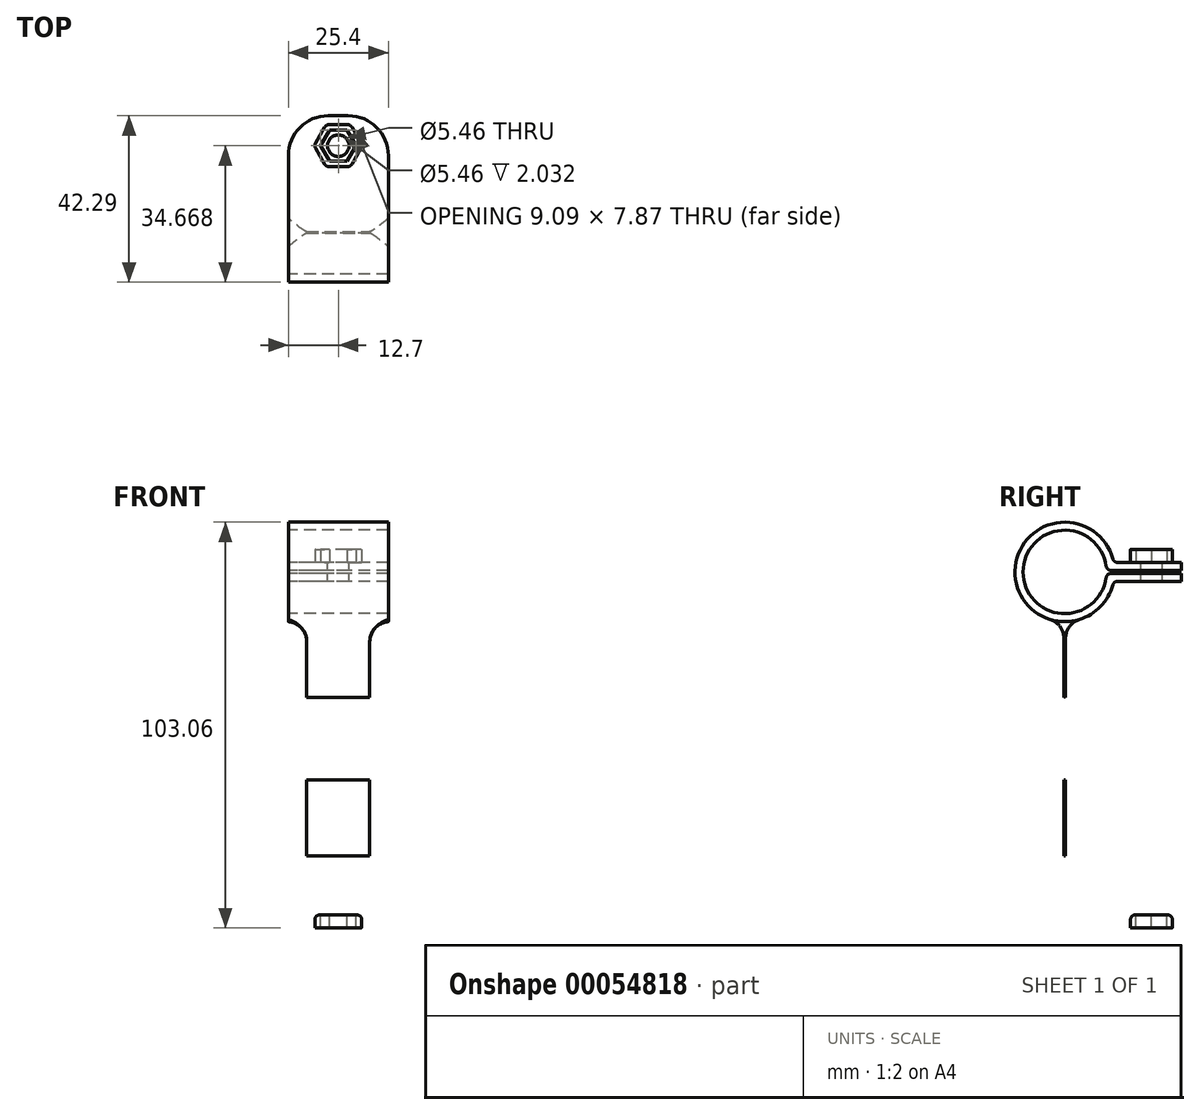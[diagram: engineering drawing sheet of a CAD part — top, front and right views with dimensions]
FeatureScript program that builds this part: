
annotation { "Feature Type Name" : "Feature", "Feature Type Description" : "" }
export const myFeature = defineFeature(function(context is Context, id is Id, definition is map)
    precondition{}
    {
        {
            var Q0;
            Q0=qCreatedBy(makeId("Front.planeOp"),FACE);
            var sketch = newSketch(context, id + "F0", { "sketchPlane" : qUnion([Q0])});
            skLineSegment(sketch, "E0", {"start": v(-8, -29.85) * mm, "end": v(-8, 29.84) * mm});
            skLineSegment(sketch, "E1", {"start": v(-8, 29.85) * mm, "end": v(8, 29.85) * mm});
            skLineSegment(sketch, "E2", {"start": v(8, 29.84) * mm, "end": v(8, -29.85) * mm});
            skCircle(sketch, "E3", {"center": v(0, 0) * mm, "radius": 2.54 * mm});
            skLineSegment(sketch, "E4", {"start": v(-8, -29.85) * mm, "end": v(8, -29.85) * mm});
            skLineSegment(sketch, "E5", {"start": v(-8, 0) * mm, "end": v(8, 0) * mm, "construction": true});
            skSolve(sketch);
        }
        {
            var Q0;
            Q0=qSketchRegion(id+"F0",true);
            extrude(context, id + "F1", {"entities" : qUnion([Q0]), "depth" : ((.116 * 2 + .13) / 2) * mm, "hasSecondDirection" : true, "secondDirectionOppositeDirection" : true, "secondDirectionDepth" : ((.116 * 2 + .13) / 2) * mm});
        }
        {
            var Q0;
            Q0=qCreatedBy(makeId("Right.planeOp"),FACE);
            var sketch = newSketch(context, id + "F2", { "sketchPlane" : qUnion([Q0])});
            skArc(sketch, "E6", {"start": v(10.5, 43.83) * mm, "mid": v(-10.6, 42.35) * mm, "end": v(10.5, 40.88) * mm});
            skArc(sketch, "E7", {"start": v(12.19, 45.7) * mm, "mid": v(-12.64, 42.35) * mm, "end": v(12.19, 39) * mm});
            skLineSegment(sketch, "E8.bottom", {"start": v(13.4, 44.77) * mm, "end": v(29.65, 44.77) * mm});
            skLineSegment(sketch, "E8.top", {"start": v(13.4, 39.94) * mm, "end": v(29.65, 39.94) * mm});
            skLineSegment(sketch, "E8.right", {"start": v(29.65, 44.77) * mm, "end": v(29.65, 42.74) * mm});
            skLineSegment(sketch, "E9.bottom", {"start": v(11.76, 42.74) * mm, "end": v(29.65, 42.74) * mm});
            skLineSegment(sketch, "E9.top", {"start": v(11.76, 41.97) * mm, "end": v(29.65, 41.97) * mm});
            skLineSegment(sketch, "E10.trimOffspring", {"start": v(29.65, 41.97) * mm, "end": v(29.65, 39.94) * mm});
            skLineSegment(sketch, "E11", {"start": v(0, 42.35) * mm, "end": v(10.6, 42.35) * mm, "construction": true});
            skLineSegment(sketch, "E12", {"start": v(10.6, 42.74) * mm, "end": v(10.6, 41.97) * mm, "construction": true});
            skPoint(sketch, "E13.visualSharp", {"position": v(10.6, 42.74) * mm});
            skArc(sketch, "E13.filletArc", {"start": v(10.5, 43.83) * mm, "mid": v(10.93, 43.05) * mm, "end": v(11.76, 42.74) * mm});
            skPoint(sketch, "E14.visualSharp", {"position": v(10.6, 41.97) * mm});
            skArc(sketch, "E14.filletArc", {"start": v(11.76, 41.97) * mm, "mid": v(10.93, 41.66) * mm, "end": v(10.5, 40.88) * mm});
            skPoint(sketch, "E15.visualSharp", {"position": v(12.4, 44.77) * mm});
            skArc(sketch, "E15.filletArc", {"start": v(12.19, 45.7) * mm, "mid": v(12.64, 45.03) * mm, "end": v(13.4, 44.77) * mm});
            skPoint(sketch, "E16.visualSharp", {"position": v(12.4, 39.94) * mm});
            skArc(sketch, "E16.filletArc", {"start": v(13.4, 39.94) * mm, "mid": v(12.64, 39.68) * mm, "end": v(12.19, 39) * mm});
            skLineSegment(sketch, "E17", {"start": v(0, 0) * mm, "end": v(-15.6, 0) * mm, "construction": true});
            skArc(sketch, "E18.MirrorCS", {"start": v(13.4, -39.94) * mm, "mid": v(12.64, -39.68) * mm, "end": v(12.19, -39) * mm});
            skArc(sketch, "E19.MirrorCS", {"start": v(12.19, -45.7) * mm, "mid": v(12.64, -45.03) * mm, "end": v(13.4, -44.77) * mm});
            skLineSegment(sketch, "E20.MirrorCS", {"start": v(0, -42.35) * mm, "end": v(10.6, -42.35) * mm, "construction": true});
            skLineSegment(sketch, "E21.MirrorCS", {"start": v(10.6, -42.74) * mm, "end": v(10.6, -41.97) * mm, "construction": true});
            skArc(sketch, "E22.MirrorCS", {"start": v(10.5, -43.83) * mm, "mid": v(10.93, -43.05) * mm, "end": v(11.76, -42.74) * mm});
            skArc(sketch, "E23.MirrorCS", {"start": v(11.76, -41.97) * mm, "mid": v(10.93, -41.66) * mm, "end": v(10.5, -40.88) * mm});
            skLineSegment(sketch, "E24.MirrorCS", {"start": v(29.65, -41.97) * mm, "end": v(29.65, -39.94) * mm});
            skLineSegment(sketch, "E25.MirrorCS", {"start": v(29.65, -44.77) * mm, "end": v(29.65, -42.74) * mm});
            skPoint(sketch, "E26.MirrorP", {"position": v(10.6, -41.97) * mm});
            skPoint(sketch, "E27.MirrorP", {"position": v(12.4, -44.77) * mm});
            skPoint(sketch, "E28.MirrorP", {"position": v(12.4, -39.94) * mm});
            skPoint(sketch, "E29.MirrorP", {"position": v(10.6, -42.74) * mm});
            skLineSegment(sketch, "E30.MirrorCS", {"start": v(11.76, -42.74) * mm, "end": v(29.65, -42.74) * mm});
            skLineSegment(sketch, "E31.MirrorCS", {"start": v(11.76, -41.97) * mm, "end": v(29.65, -41.97) * mm});
            skArc(sketch, "E32.MirrorCS", {"start": v(10.5, -43.83) * mm, "mid": v(-10.6, -42.35) * mm, "end": v(10.5, -40.88) * mm});
            skArc(sketch, "E33.MirrorCS", {"start": v(12.19, -45.7) * mm, "mid": v(-12.64, -42.35) * mm, "end": v(12.19, -39) * mm});
            skLineSegment(sketch, "E34.MirrorCS", {"start": v(13.4, -44.77) * mm, "end": v(29.65, -44.77) * mm});
            skLineSegment(sketch, "E35.MirrorCS", {"start": v(13.4, -39.94) * mm, "end": v(29.65, -39.94) * mm});
            skSolve(sketch);
        }
        {
            var Q0;
            Q0=makeQuery(id+"F2.imprint","IMPRINT",FACE,{"disambiguationData":[TD([[makeQuery(id+"F2.imprint","IMPRINT",EDGE,{"derivedFrom":sQuery(id+"F2.wireOp",EDGE,"E6")}),-1.0]])]});
            var Q1;
            Q1=makeQuery(id+"F2.imprint","IMPRINT",FACE,{"disambiguationData":[TD([[makeQuery(id+"F2.imprint","IMPRINT",EDGE,{"derivedFrom":sQuery(id+"F2.wireOp",EDGE,"E18.MirrorCS")}),1.0]])]});
            extrude(context, id + "F3", {"entities" : qUnion([Q0, Q1]), "operationType" : NewBodyOperationType.ADD, "depth" : 12.7 * mm, "hasSecondDirection" : true, "secondDirectionOppositeDirection" : true, "secondDirectionDepth" : 12.7 * mm});
        }
        {
            var Q0;
            Q0=qCreatedBy(makeId("Right.planeOp"),FACE);
            var sketch = newSketch(context, id + "F4", { "sketchPlane" : qUnion([Q0])});
            skLineSegment(sketch, "E36.left", {"start": v(-1.65, 8.9) * mm, "end": v(-1.65, -8.9) * mm});
            skLineSegment(sketch, "E36.right", {"start": v(1.65, 8.9) * mm, "end": v(1.65, -8.89) * mm});
            skArc(sketch, "E37", {"start": v(1.65, 8.9) * mm, "mid": v(0, 10.54) * mm, "end": v(-1.65, 8.9) * mm});
            skPoint(sketch, "E37.first.point", {"position": v(-1.65, 8.9) * mm});
            skPoint(sketch, "E37.third.point", {"position": v(1.65, 8.9) * mm});
            skLineSegment(sketch, "E38", {"start": v(0, -8.9) * mm, "end": v(0, 0) * mm, "construction": true});
            skArc(sketch, "E39", {"start": v(-1.65, -8.9) * mm, "mid": v(0, -10.54) * mm, "end": v(1.65, -8.89) * mm});
            skLineSegment(sketch, "E40", {"start": v(0, 0) * mm, "end": v(0, 8.9) * mm, "construction": true});
            skSolve(sketch);
        }
        {
            var Q0;
            Q0=qSketchRegion(id+"F4",true);
            extrude(context, id + "F5", {"entities" : qUnion([Q0]), "operationType" : NewBodyOperationType.REMOVE, "endBound" : BoundingType.THROUGH_ALL, "oppositeDirection" : true, "depth" : 25.4 * mm, "hasSecondDirection" : true, "secondDirectionBound" : BoundingType.THROUGH_ALL, "secondDirectionOppositeDirection" : false, "secondDirectionDepth" : 25.4 * mm});
        }
        {
            var Q0;
            Q0=makeQuery(id+"F3.boolean.opBoolean","INTERSECT",EDGE,{"derivedFrom":[makeQuery(id+"F1.opExtrude","CAP_FACE",FACE,{"disambiguationData":[OSD([sQuery(id+"F0.wireOp",EDGE,"32f0cda4-ce3b-4ee3-906d-ccfbde551a43"),sQuery(id+"F0.wireOp",EDGE,"E0"),sQuery(id+"F0.wireOp",EDGE,"E1"),sQuery(id+"F0.wireOp",EDGE,"E2"),sQuery(id+"F0.wireOp",EDGE,"E3")])],"isStart":true}),makeQuery(id+"F3.opExtrude","SWEPT_FACE",FACE,{"disambiguationData":[OSD([sQuery(id+"F2.wireOp",EDGE,"E7")])]})]});
            var Q1;
            Q1=makeQuery(id+"F3.boolean.opBoolean","INTERSECT",EDGE,{"derivedFrom":[makeQuery(id+"F1.opExtrude","CAP_FACE",FACE,{"disambiguationData":[OSD([sQuery(id+"F0.wireOp",EDGE,"32f0cda4-ce3b-4ee3-906d-ccfbde551a43"),sQuery(id+"F0.wireOp",EDGE,"E0"),sQuery(id+"F0.wireOp",EDGE,"E1"),sQuery(id+"F0.wireOp",EDGE,"E2"),sQuery(id+"F0.wireOp",EDGE,"E3")])],"isStart":false}),makeQuery(id+"F3.opExtrude","SWEPT_FACE",FACE,{"disambiguationData":[OSD([sQuery(id+"F2.wireOp",EDGE,"E7")])]})]});
            var Q2;
            Q2=makeQuery(id+"F3.boolean.opBoolean","INTERSECT",EDGE,{"derivedFrom":[makeQuery(id+"F1.opExtrude","SWEPT_FACE",FACE,{"disambiguationData":[OSD([sQuery(id+"F0.wireOp",EDGE,"E2")])]}),makeQuery(id+"F3.opExtrude","SWEPT_FACE",FACE,{"disambiguationData":[OSD([sQuery(id+"F2.wireOp",EDGE,"E7")])]})]});
            var Q3;
            Q3=makeQuery(id+"F3.boolean.opBoolean","INTERSECT",EDGE,{"derivedFrom":[makeQuery(id+"F1.opExtrude","SWEPT_FACE",FACE,{"disambiguationData":[OSD([sQuery(id+"F0.wireOp",EDGE,"E0")])]}),makeQuery(id+"F3.opExtrude","SWEPT_FACE",FACE,{"disambiguationData":[OSD([sQuery(id+"F2.wireOp",EDGE,"E7")])]})]});
            var Q4;
            Q4=makeQuery(id+"F3.boolean.opBoolean","INTERSECT",EDGE,{"derivedFrom":[makeQuery(id+"F1.opExtrude","CAP_FACE",FACE,{"disambiguationData":[OSD([sQuery(id+"F0.wireOp",EDGE,"E0"),sQuery(id+"F0.wireOp",EDGE,"E1"),sQuery(id+"F0.wireOp",EDGE,"E2"),sQuery(id+"F0.wireOp",EDGE,"E3"),sQuery(id+"F0.wireOp",EDGE,"E4")])],"isStart":false}),makeQuery(id+"F3.opExtrude","SWEPT_FACE",FACE,{"disambiguationData":[OSD([sQuery(id+"F2.wireOp",EDGE,"E33.MirrorCS")])]})]});
            var Q5;
            Q5=makeQuery(id+"F3.boolean.opBoolean","INTERSECT",EDGE,{"derivedFrom":[makeQuery(id+"F1.opExtrude","SWEPT_FACE",FACE,{"disambiguationData":[OSD([sQuery(id+"F0.wireOp",EDGE,"E2")])]}),makeQuery(id+"F3.opExtrude","SWEPT_FACE",FACE,{"disambiguationData":[OSD([sQuery(id+"F2.wireOp",EDGE,"E33.MirrorCS")])]})]});
            var Q6;
            Q6=makeQuery(id+"F3.boolean.opBoolean","INTERSECT",EDGE,{"derivedFrom":[makeQuery(id+"F1.opExtrude","CAP_FACE",FACE,{"disambiguationData":[OSD([sQuery(id+"F0.wireOp",EDGE,"E0"),sQuery(id+"F0.wireOp",EDGE,"E1"),sQuery(id+"F0.wireOp",EDGE,"E2"),sQuery(id+"F0.wireOp",EDGE,"E3"),sQuery(id+"F0.wireOp",EDGE,"E4")])],"isStart":true}),makeQuery(id+"F3.opExtrude","SWEPT_FACE",FACE,{"disambiguationData":[OSD([sQuery(id+"F2.wireOp",EDGE,"E33.MirrorCS")])]})]});
            var Q7;
            Q7=makeQuery(id+"F3.boolean.opBoolean","INTERSECT",EDGE,{"derivedFrom":[makeQuery(id+"F1.opExtrude","SWEPT_FACE",FACE,{"disambiguationData":[OSD([sQuery(id+"F0.wireOp",EDGE,"E0")])]}),makeQuery(id+"F3.opExtrude","SWEPT_FACE",FACE,{"disambiguationData":[OSD([sQuery(id+"F2.wireOp",EDGE,"E33.MirrorCS")])]})]});
            fillet(context, id + "F6", {"entities" : qUnion([Q0, Q1, Q2, Q3, Q4, Q5, Q6, Q7]), "radius" : 5.08 * mm, "tangentPropagation" : true, "allowEdgeOverflow" : false});
        }
        {
            var Q0;
            Q0=makeQuery(id+"F3.opExtrude","CAP_EDGE",EDGE,{"disambiguationData":[OSD([sQuery(id+"F2.wireOp",EDGE,"E8.right")])],"isStart":false});
            var Q1;
            Q1=makeQuery(id+"F3.opExtrude","CAP_EDGE",EDGE,{"disambiguationData":[OSD([sQuery(id+"F2.wireOp",EDGE,"E8.right")])],"isStart":true});
            var Q2;
            Q2=makeQuery(id+"F3.opExtrude","CAP_EDGE",EDGE,{"disambiguationData":[OSD([sQuery(id+"F2.wireOp",EDGE,"E10.trimOffspring")])],"isStart":true});
            var Q3;
            Q3=makeQuery(id+"F3.opExtrude","CAP_EDGE",EDGE,{"disambiguationData":[OSD([sQuery(id+"F2.wireOp",EDGE,"E10.trimOffspring")])],"isStart":false});
            var Q4;
            Q4=makeQuery(id+"F3.opExtrude","CAP_EDGE",EDGE,{"disambiguationData":[OSD([sQuery(id+"F2.wireOp",EDGE,"E24.MirrorCS")])],"isStart":false});
            var Q5;
            Q5=makeQuery(id+"F3.opExtrude","CAP_EDGE",EDGE,{"disambiguationData":[OSD([sQuery(id+"F2.wireOp",EDGE,"E25.MirrorCS")])],"isStart":false});
            var Q6;
            Q6=makeQuery(id+"F3.opExtrude","CAP_EDGE",EDGE,{"disambiguationData":[OSD([sQuery(id+"F2.wireOp",EDGE,"E25.MirrorCS")])],"isStart":true});
            var Q7;
            Q7=makeQuery(id+"F3.opExtrude","CAP_EDGE",EDGE,{"disambiguationData":[OSD([sQuery(id+"F2.wireOp",EDGE,"E24.MirrorCS")])],"isStart":true});
            fillet(context, id + "F7", {"entities" : qUnion([Q0, Q1, Q2, Q3, Q4, Q5, Q6, Q7]), "radius" : 10.16 * mm, "tangentPropagation" : true, "allowEdgeOverflow" : false});
        }
        {
            var Q0;
            Q0=makeQuery(id+"F3.opExtrude","SWEPT_FACE",FACE,{"disambiguationData":[OSD([sQuery(id+"F2.wireOp",EDGE,"E8.bottom")])]});
            var sketch = newSketch(context, id + "F8", { "sketchPlane" : qUnion([Q0])});
            skCircle(sketch, "E41.cCircle", {"center": v(0, 22.03) * mm, "radius": 3.94 * mm, "construction": true});
            skLineSegment(sketch, "E41.0", {"start": v(2.27, 18.1) * mm, "end": v(-2.27, 18.1) * mm});
            skLineSegment(sketch, "E41.1", {"start": v(-2.27, 18.1) * mm, "end": v(-4.55, 22.03) * mm});
            skLineSegment(sketch, "E41.2", {"start": v(-4.55, 22.03) * mm, "end": v(-2.27, 25.96) * mm});
            skLineSegment(sketch, "E41.3", {"start": v(-2.27, 25.96) * mm, "end": v(2.27, 25.96) * mm});
            skLineSegment(sketch, "E41.4", {"start": v(2.27, 25.96) * mm, "end": v(4.55, 22.03) * mm});
            skLineSegment(sketch, "E41.5", {"start": v(4.55, 22.03) * mm, "end": v(2.27, 18.1) * mm});
            skPoint(sketch, "E41.0.midPoint", {"position": v(0, 18.1) * mm});
            skCircle(sketch, "E42.cCircle", {"center": v(0, 22.03) * mm, "radius": 5.33 * mm, "construction": true});
            skLineSegment(sketch, "E42.0", {"start": v(3.08, 16.7) * mm, "end": v(-3.08, 16.7) * mm});
            skLineSegment(sketch, "E42.1", {"start": v(-3.08, 16.7) * mm, "end": v(-6.16, 22.03) * mm});
            skLineSegment(sketch, "E42.2", {"start": v(-6.16, 22.03) * mm, "end": v(-3.08, 27.36) * mm});
            skLineSegment(sketch, "E42.3", {"start": v(-3.08, 27.36) * mm, "end": v(3.08, 27.36) * mm});
            skLineSegment(sketch, "E42.4", {"start": v(3.08, 27.36) * mm, "end": v(6.16, 22.03) * mm});
            skLineSegment(sketch, "E42.5", {"start": v(6.16, 22.03) * mm, "end": v(3.08, 16.7) * mm});
            skPoint(sketch, "E42.0.midPoint", {"position": v(0, 16.7) * mm});
            skLineSegment(sketch, "E43", {"start": v(0, 29.65) * mm, "end": v(0, 22.03) * mm, "construction": true});
            skSolve(sketch);
        }
        {
            var Q0;
            Q0=makeQuery(id+"F8.imprint","IMPRINT",FACE,{"disambiguationData":[TD([[makeQuery(id+"F8.imprint","IMPRINT",EDGE,{"derivedFrom":sQuery(id+"F8.wireOp",EDGE,"E41.0")}),1.0]])]});
            extrude(context, id + "F9", {"entities" : qUnion([Q0]), "depth" : 3.3 * mm});
        }
        {
            var Q0;
            Q0=makeQuery(id+"F9.opExtrude","SWEPT_EDGE",EDGE,{"disambiguationData":[OSD([sQuery(id+"F8.wireOp",EDGE,"E42.2"),sQuery(id+"F8.wireOp",EDGE,"E42.3")])]});
            var Q1;
            Q1=makeQuery(id+"F9.opExtrude","SWEPT_EDGE",EDGE,{"disambiguationData":[OSD([sQuery(id+"F8.wireOp",EDGE,"E42.1"),sQuery(id+"F8.wireOp",EDGE,"E42.2")])]});
            var Q2;
            Q2=makeQuery(id+"F9.opExtrude","SWEPT_EDGE",EDGE,{"disambiguationData":[OSD([sQuery(id+"F8.wireOp",EDGE,"E42.0"),sQuery(id+"F8.wireOp",EDGE,"E42.1")])]});
            var Q3;
            Q3=makeQuery(id+"F9.opExtrude","SWEPT_EDGE",EDGE,{"disambiguationData":[OSD([sQuery(id+"F8.wireOp",EDGE,"E42.3"),sQuery(id+"F8.wireOp",EDGE,"E42.4")])]});
            var Q4;
            Q4=makeQuery(id+"F9.opExtrude","SWEPT_EDGE",EDGE,{"disambiguationData":[OSD([sQuery(id+"F8.wireOp",EDGE,"E42.4"),sQuery(id+"F8.wireOp",EDGE,"E42.5")])]});
            var Q5;
            Q5=makeQuery(id+"F9.opExtrude","SWEPT_EDGE",EDGE,{"disambiguationData":[OSD([sQuery(id+"F8.wireOp",EDGE,"E42.0"),sQuery(id+"F8.wireOp",EDGE,"E42.5")])]});
            fillet(context, id + "F10", {"entities" : qUnion([Q0, Q1, Q2, Q3, Q4, Q5]), "radius" : 1.27 * mm, "tangentPropagation" : true, "allowEdgeOverflow" : false});
        }
        {
            var Q0;
            Q0=makeQuery(id+"F9.opExtrude","SWEPT_BODY",BODY,{"disambiguationData":[OSD([sQuery(id+"F8.wireOp",EDGE,"E41.0"),sQuery(id+"F8.wireOp",EDGE,"E41.1"),sQuery(id+"F8.wireOp",EDGE,"E41.2"),sQuery(id+"F8.wireOp",EDGE,"E41.3"),sQuery(id+"F8.wireOp",EDGE,"E41.4"),sQuery(id+"F8.wireOp",EDGE,"E41.5"),sQuery(id+"F8.wireOp",EDGE,"E42.0"),sQuery(id+"F8.wireOp",EDGE,"E42.1"),sQuery(id+"F8.wireOp",EDGE,"E42.2"),sQuery(id+"F8.wireOp",EDGE,"E42.3"),sQuery(id+"F8.wireOp",EDGE,"E42.4"),sQuery(id+"F8.wireOp",EDGE,"E42.5")])]});
            var Q1;
            Q1=qCreatedBy(makeId("Top.planeOp"),FACE);
            mirror(context, id + "F11", {"operationType" : NewBodyOperationType.ADD, "entities" : qUnion([Q0]), "mirrorPlane" : qUnion([Q1])});
        }
        {
            var Q0;
            Q0=makeQuery(id+"F9.opExtrude","CAP_EDGE",EDGE,{"disambiguationData":[OSD([sQuery(id+"F8.wireOp",EDGE,"E42.5")])],"isStart":true});
            var Q1;
            Q1=makeQuery(id+"F11.opPattern","COPY",EDGE,{"derivedFrom":makeQuery(id+"F9.opExtrude","CAP_EDGE",EDGE,{"disambiguationData":[OSD([sQuery(id+"F8.wireOp",EDGE,"E42.4")])],"isStart":true}),"instanceName":"1"});
            fillet(context, id + "F12", {"entities" : qUnion([Q0, Q1]), "radius" : 1.27 * mm, "tangentPropagation" : true, "allowEdgeOverflow" : false});
        }
        {
            var Q0;
            Q0=makeQuery(id+"F9.boolean.opBoolean","SPLIT",FACE,{"disambiguationData":[TD([makeQuery(id+"F9.opExtrude","SWEPT_FACE",FACE,{"disambiguationData":[OSD([sQuery(id+"F8.wireOp",EDGE,"E41.0")])]})])],"derivedFrom":makeQuery(id+"F3.opExtrude","SWEPT_FACE",FACE,{"disambiguationData":[OSD([sQuery(id+"F2.wireOp",EDGE,"E8.bottom")])]})});
            var sketch = newSketch(context, id + "F13", { "sketchPlane" : qUnion([Q0])});
            skCircle(sketch, "E44", {"center": v(0, 22.03) * mm, "radius": 2.73 * mm});
            skSolve(sketch);
        }
        {
            var Q0;
            Q0=qSketchRegion(id+"F13",true);
            var Q1;
            Q1=makeQuery(id+"F3.opExtrude","SWEPT_FACE",FACE,{"disambiguationData":[OSD([sQuery(id+"F2.wireOp",EDGE,"E8.top")])]});
            extrude(context, id + "F14", {"entities" : qUnion([Q0]), "operationType" : NewBodyOperationType.REMOVE, "endBound" : BoundingType.THROUGH_ALL, "oppositeDirection" : true, "endBoundEntityFace" : qUnion([Q1]), "depth" : 25.4 * mm});
        }
    });
